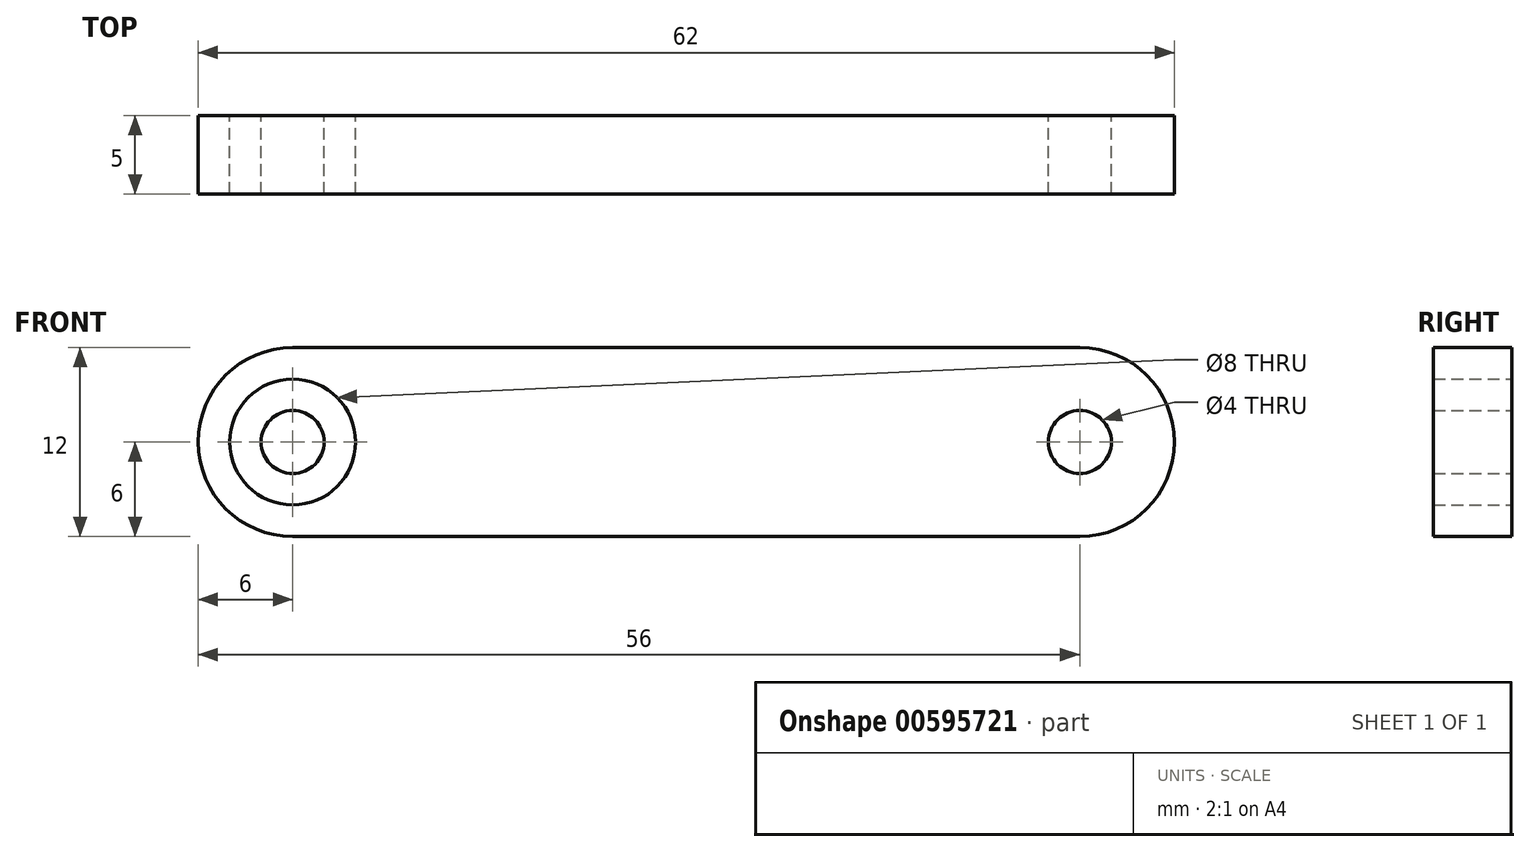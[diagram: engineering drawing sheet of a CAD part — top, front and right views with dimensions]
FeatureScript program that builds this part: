
annotation { "Feature Type Name" : "Feature", "Feature Type Description" : "" }
export const myFeature = defineFeature(function(context is Context, id is Id, definition is map)
    precondition{}
    {
        {
            var Q0;
            Q0=qCreatedBy(makeId("Front.planeOp"),FACE);
            var sketch = newSketch(context, id + "F0", { "sketchPlane" : qUnion([Q0])});
            skCircle(sketch, "E0", {"center": v(-25, 0) * mm, "radius": 2 * mm});
            skCircle(sketch, "E1", {"center": v(-25, 0) * mm, "radius": 4 * mm});
            skArc(sketch, "E2", {"start": v(-25, 6) * mm, "mid": v(-31, 0) * mm, "end": v(-25, -6) * mm});
            skLineSegment(sketch, "E3", {"start": v(-25.03, 6) * mm, "end": v(0, 6) * mm});
            skLineSegment(sketch, "E4", {"start": v(-25, -6) * mm, "end": v(0, -6) * mm});
            skCircle(sketch, "E5.MirrorC", {"center": v(25, 0) * mm, "radius": 2 * mm});
            skCircle(sketch, "E6.MirrorC", {"center": v(25, 0) * mm, "radius": 4 * mm});
            skLineSegment(sketch, "E7.MirrorCS", {"start": v(25.03, 6) * mm, "end": v(0, 6) * mm});
            skLineSegment(sketch, "E8.MirrorCS", {"start": v(25, -6) * mm, "end": v(0, -6) * mm});
            skArc(sketch, "E9.MirrorCS", {"start": v(25, 6) * mm, "mid": v(31, 0) * mm, "end": v(25, -6) * mm});
            skSolve(sketch);
        }
        {
            var Q0;
            Q0 = qSketchRegion(id + "F0", true);
            var Q1;
            Q1=makeQuery(id+"F0.imprint","IMPRINT",FACE,{"disambiguationData":[TD([[makeQuery(id+"F0.imprint","IMPRINT",EDGE,{"derivedFrom":sQuery(id+"F0.wireOp",EDGE,"E0")}),1.0]])]});
            var Q2;
            Q2=makeQuery(id+"F0.imprint","IMPRINT",FACE,{"disambiguationData":[TD([[makeQuery(id+"F0.imprint","IMPRINT",EDGE,{"derivedFrom":sQuery(id+"F0.wireOp",EDGE,"E5.MirrorC")}),-1.0]])]});
            extrude(context, id + "F1", {"entities" : qUnion([Q0, Q1, Q2]), "depth" : 5 * mm, "offsetDistance" : 25 * mm});
        }
    });
